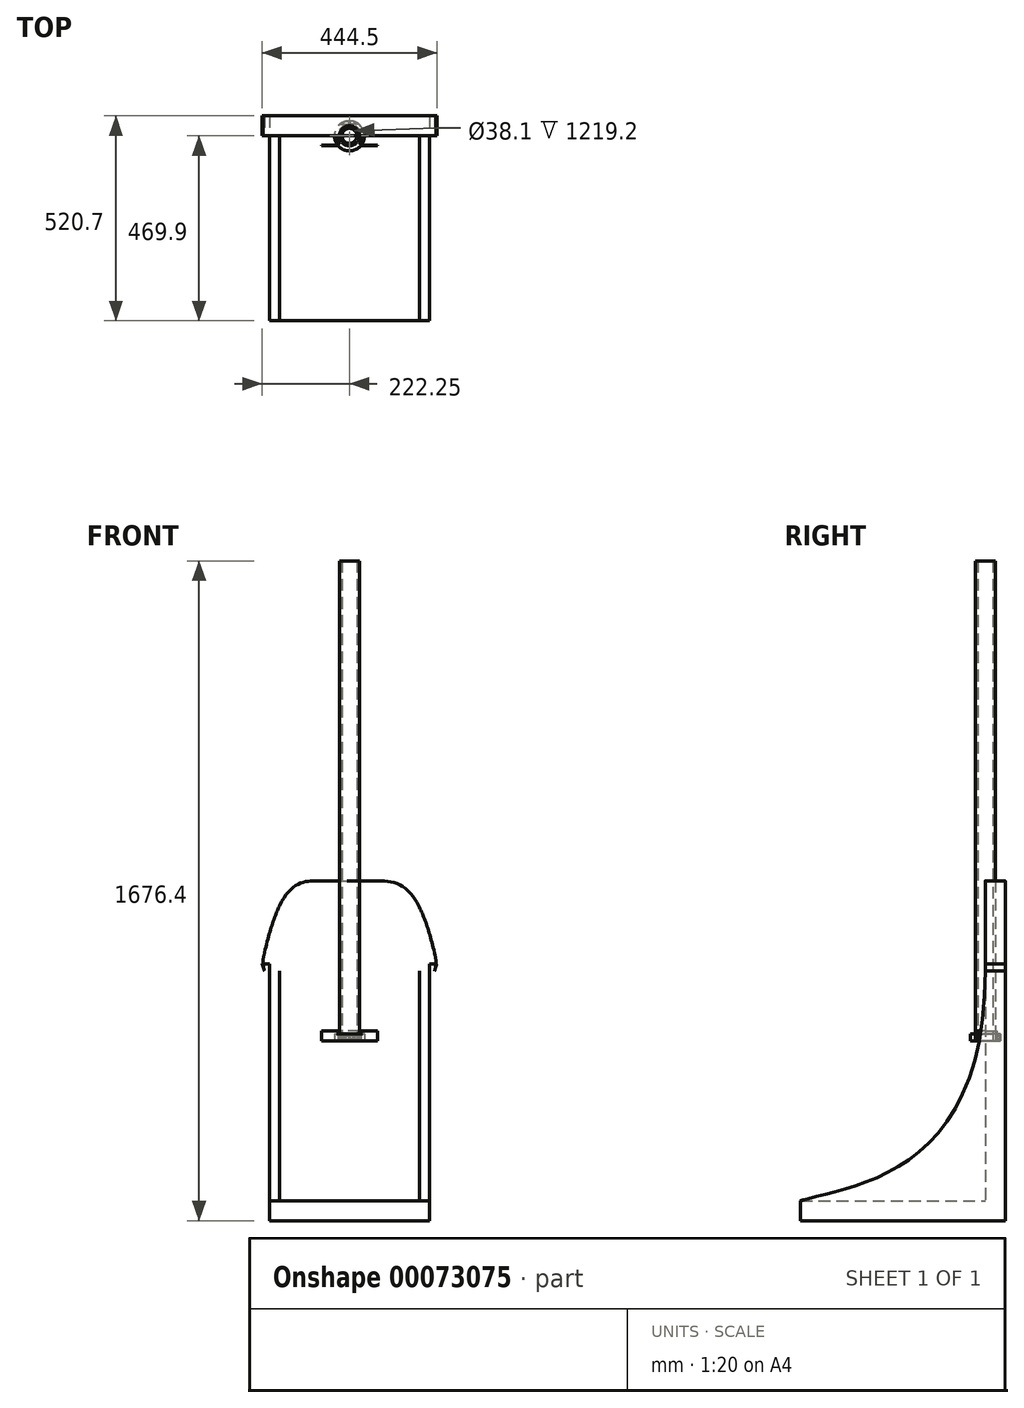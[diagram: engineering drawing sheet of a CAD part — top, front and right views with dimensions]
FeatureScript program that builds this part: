
annotation { "Feature Type Name" : "Feature", "Feature Type Description" : "" }
export const myFeature = defineFeature(function(context is Context, id is Id, definition is map)
    precondition{}
    {
        {
            var Q0;
            Q0=qCreatedBy(makeId("Top.planeOp"),FACE);
            var sketch = newSketch(context, id + "F0", { "sketchPlane" : qUnion([Q0])});
            skCircle(sketch, "E0", {"center": v(0, 0) * mm, "radius": 25.4 * mm});
            skCircle(sketch, "E1", {"center": v(0, 0) * mm, "radius": 19.05 * mm});
            skLineSegment(sketch, "E2", {"start": v(-26.99, 0) * mm, "end": v(-26.99, -19.05) * mm});
            skLineSegment(sketch, "E3", {"start": v(26.99, 0) * mm, "end": v(26.99, -19.05) * mm});
            skLineSegment(sketch, "E4", {"start": v(33.34, -25.4) * mm, "end": v(71.44, -25.4) * mm});
            skLineSegment(sketch, "E5", {"start": v(-33.34, -25.4) * mm, "end": v(-71.44, -25.4) * mm});
            skArc(sketch, "E6", {"start": v(-26.99, 0) * mm, "mid": v(0, 26.99) * mm, "end": v(26.99, 0) * mm});
            skPoint(sketch, "E7.visualSharp", {"position": v(-26.99, -25.4) * mm});
            skArc(sketch, "E7.filletArc", {"start": v(-33.34, -25.4) * mm, "mid": v(-28.85, -23.54) * mm, "end": v(-26.99, -19.05) * mm});
            skPoint(sketch, "E8.visualSharp", {"position": v(26.99, -25.4) * mm});
            skArc(sketch, "E8.filletArc", {"start": v(26.99, -19.05) * mm, "mid": v(28.85, -23.54) * mm, "end": v(33.34, -25.4) * mm});
            skArc(sketch, "E9.1", {"start": v(33.14, -19.05) * mm, "mid": v(33.2, -19.19) * mm, "end": v(33.34, -19.24) * mm});
            skArc(sketch, "E9.4", {"start": v(-33.34, -19.24) * mm, "mid": v(-33.2, -19.19) * mm, "end": v(-33.14, -19.05) * mm});
            skLineSegment(sketch, "E10.0", {"start": v(33.34, -23.16) * mm, "end": v(71.44, -23.16) * mm});
            skArc(sketch, "E10.1", {"start": v(29.23, -19.05) * mm, "mid": v(30.43, -21.95) * mm, "end": v(33.34, -23.16) * mm});
            skLineSegment(sketch, "E10.2", {"start": v(29.23, 0) * mm, "end": v(29.23, -19.05) * mm});
            skLineSegment(sketch, "E10.3", {"start": v(-33.34, -23.16) * mm, "end": v(-71.44, -23.16) * mm});
            skArc(sketch, "E10.4", {"start": v(-33.34, -23.16) * mm, "mid": v(-30.43, -21.95) * mm, "end": v(-29.23, -19.05) * mm});
            skLineSegment(sketch, "E10.5", {"start": v(-29.23, 0) * mm, "end": v(-29.23, -19.05) * mm});
            skArc(sketch, "E10.6", {"start": v(-29.23, 0) * mm, "mid": v(0, 29.23) * mm, "end": v(29.23, 0) * mm});
            skLineSegment(sketch, "E11", {"start": v(71.44, -23.16) * mm, "end": v(71.44, -25.4) * mm});
            skLineSegment(sketch, "E12", {"start": v(-71.44, -23.16) * mm, "end": v(-71.44, -25.4) * mm});
            skSolve(sketch);
        }
        {
            var Q0;
            Q0=makeQuery(id+"F0.imprint","IMPRINT",FACE,{"disambiguationData":[TD([[makeQuery(id+"F0.imprint","IMPRINT",EDGE,{"derivedFrom":sQuery(id+"F0.wireOp",EDGE,"E0")}),1.0]])]});
            extrude(context, id + "F1", {"entities" : qUnion([Q0]), "depth" : 1219.2 * mm});
        }
        {
            var Q0;
            Q0=makeQuery(id+"F0.imprint","IMPRINT",FACE,{"disambiguationData":[TD([[makeQuery(id+"F0.imprint","IMPRINT",EDGE,{"derivedFrom":sQuery(id+"F0.wireOp",EDGE,"E2")}),-1.0]])]});
            extrude(context, id + "F2", {"entities" : qUnion([Q0]), "depth" : 25.4 * mm});
        }
        {
            var Q0;
            Q0=qCreatedBy(makeId("Top.planeOp"),FACE);
            var sketch = newSketch(context, id + "F3", { "sketchPlane" : qUnion([Q0])});
            skArc(sketch, "E13", {"start": v(-1.21, 38.08) * mm, "mid": v(0, -38.1) * mm, "end": v(1.21, 38.08) * mm});
            skArc(sketch, "E14", {"start": v(-1.21, 25.37) * mm, "mid": v(0, -25.4) * mm, "end": v(1.21, 25.37) * mm});
            skLineSegment(sketch, "E15", {"start": v(1.21, 38.08) * mm, "end": v(1.21, 25.37) * mm});
            skLineSegment(sketch, "E16", {"start": v(-1.21, 38.08) * mm, "end": v(-1.21, 25.37) * mm});
            skSolve(sketch);
        }
        {
            var Q0;
            Q0=makeQuery(id+"F3.imprint","IMPRINT",FACE,{"disambiguationData":[TD([[makeQuery(id+"F3.imprint","IMPRINT",EDGE,{"derivedFrom":sQuery(id+"F3.wireOp",EDGE,"E13")}),1.0]])]});
            extrude(context, id + "F4", {"entities" : qUnion([Q0]), "depth" : 17.48 * mm});
        }
        {
            var Q0;
            Q0=qCreatedBy(makeId("Right.planeOp"),FACE);
            var sketch = newSketch(context, id + "F5", { "sketchPlane" : qUnion([Q0])});
            skCircle(sketch, "E17", {"center": v(33.29, 8.78) * mm, "radius": 3.81 * mm});
            skPoint(sketch, "E17.first.point", {"position": v(37.1, 8.75) * mm});
            skPoint(sketch, "E17.second.point", {"position": v(29.48, 8.75) * mm});
            skPoint(sketch, "E17.third.point", {"position": v(30.58, 11.46) * mm});
            skSolve(sketch);
        }
        {
            var Q0;
            Q0=sQuery(id+"F5.wireOp",VERTEX,"E17.center");
            var Q1;
            Q1=makeQuery(id+"F4.opExtrude","SWEPT_BODY",BODY,{"disambiguationData":[OSD([sQuery(id+"F3.wireOp",EDGE,"E13"),sQuery(id+"F3.wireOp",EDGE,"E14"),sQuery(id+"F3.wireOp",EDGE,"E15"),sQuery(id+"F3.wireOp",EDGE,"E16")])]});
            hole(context, id + "F6", {"style" : HoleStyle.SIMPLE, "holeDiameter" : 7.62 * mm, "endStyle" : HoleEndStyle.THROUGH, "locations" : qUnion([Q0]), "scope" : qUnion([Q1])});
        }
        {
            var Q0;
            Q0=sQuery(id+"F5.wireOp",VERTEX,"E17.center");
            var Q1;
            Q1=makeQuery(id+"F4.opExtrude","SWEPT_BODY",BODY,{"disambiguationData":[OSD([sQuery(id+"F3.wireOp",EDGE,"E13"),sQuery(id+"F3.wireOp",EDGE,"E14"),sQuery(id+"F3.wireOp",EDGE,"E15"),sQuery(id+"F3.wireOp",EDGE,"E16")])]});
            hole(context, id + "F7", {"style" : HoleStyle.SIMPLE, "holeDiameter" : 7.62 * mm, "endStyle" : HoleEndStyle.THROUGH, "oppositeDirection" : true, "locations" : qUnion([Q0]), "scope" : qUnion([Q1])});
        }
        {
            var Q0;
            Q0=qCreatedBy(makeId("Front.planeOp"),FACE);
            var sketch = newSketch(context, id + "F8", { "sketchPlane" : qUnion([Q0])});
            skLineSegment(sketch, "E18.rect.bottom", {"start": v(177.8, 406.4) * mm, "end": v(-177.8, 406.4) * mm});
            skLineSegment(sketch, "E18.rect.top", {"start": v(177.8, -406.4) * mm, "end": v(-177.8, -406.4) * mm});
            skLineSegment(sketch, "E18.rect.left", {"start": v(177.8, 406.4) * mm, "end": v(177.8, -406.4) * mm});
            skLineSegment(sketch, "E18.rect.right", {"start": v(-177.8, 406.4) * mm, "end": v(-177.8, -406.4) * mm});
            skPoint(sketch, "E18.rect.middle", {"position": v(0, 0) * mm});
            skLineSegment(sketch, "E19", {"start": v(-177.8, -406.4) * mm, "end": v(-177.8, -457.2) * mm});
            skLineSegment(sketch, "E20", {"start": v(-177.8, -457.2) * mm, "end": v(177.8, -457.2) * mm});
            skLineSegment(sketch, "E21", {"start": v(177.8, -457.2) * mm, "end": v(177.8, -406.4) * mm});
            skLineSegment(sketch, "E22", {"start": v(0, 195.28) * mm, "end": v(222.25, 195.28) * mm});
            skLineSegment(sketch, "E23", {"start": v(0, 195.28) * mm, "end": v(-222.25, 195.28) * mm});
            skFitSpline(sketch, "E24", {"points": [v(222.25, 195.28) * mm, v(177.8, -406.4) * mm], "startDerivative": vector(-133.35, -351.52) * mm, "endDerivative": vector(-44.45, -601.68) * mm});
            skFitSpline(sketch, "E25", {"points": [v(-222.25, 195.28) * mm, v(-177.8, -406.4) * mm], "startDerivative": vector(133.35, -334.43) * mm, "endDerivative": vector(44.45, -601.68) * mm});
            skFitSpline(sketch, "E26", {"points": [v(-222.25, 195.28) * mm, v(-73.91, 406.4) * mm, v(63.57, 406.4) * mm, v(222.25, 195.28) * mm], "startDerivative": vector(365.6, 1736.47) * mm, "endDerivative": vector(361.37, -1716.37) * mm});
            skArc(sketch, "E27.filletArc", {"start": v(-217.57, 216.72) * mm, "mid": v(-219.4, 197.15) * mm, "end": v(-216.17, 177.77) * mm});
            skArc(sketch, "E28.filletArc", {"start": v(216.4, 177.8) * mm, "mid": v(219.5, 197.03) * mm, "end": v(217.62, 216.4) * mm});
            skSolve(sketch);
        }
        {
            var Q0;
            {var subQ5=sQuery(id+"F8.wireOp",EDGE,"E26");var subQ6=sQuery(id+"F8.wireOp",EDGE,"E18.rect.left");var subQ7=makeQuery(id+"F8.imprint","INTERSECT",VERTEX,{"derivedFrom":[subQ6,subQ5]});Q0=makeQuery(id+"F8.imprint","IMPRINT",FACE,{"disambiguationData":[TD([[makeQuery(id+"F8.imprint","IMPRINT",EDGE,{"disambiguationData":[TD([[subQ7,-1.0]])],"derivedFrom":subQ6}),-1.0]])]});}
            var Q1;
            {var subQ0=sQuery(id+"F8.wireOp",EDGE,"E26");var subQ1=sQuery(id+"F8.wireOp",EDGE,"E18.rect.right");var subQ2=makeQuery(id+"F8.imprint","INTERSECT",VERTEX,{"derivedFrom":[subQ1,subQ0]});Q1=makeQuery(id+"F8.imprint","IMPRINT",FACE,{"disambiguationData":[TD([[makeQuery(id+"F8.imprint","IMPRINT",EDGE,{"disambiguationData":[TD([[subQ2,-1.0]])],"derivedFrom":subQ1}),-1.0]])]});}
            var Q2;
            {var subQ0=sQuery(id+"F8.wireOp",EDGE,"E25");Q2=makeQuery(id+"F8.imprint","IMPRINT",FACE,{"disambiguationData":[TD([[makeQuery(id+"F8.imprint","IMPRINT",EDGE,{"derivedFrom":subQ0}),1.0]])]});}
            var Q3;
            {var subQ6=sQuery(id+"F8.wireOp",EDGE,"E18.rect.top");Q3=makeQuery(id+"F8.imprint","IMPRINT",FACE,{"disambiguationData":[TD([[makeQuery(id+"F8.imprint","IMPRINT",EDGE,{"derivedFrom":subQ6}),-1.0]])]});}
            var Q4;
            {var subQ0=sQuery(id+"F8.wireOp",EDGE,"E26");var subQ1=sQuery(id+"F8.wireOp",EDGE,"E18.rect.left");var subQ2=makeQuery(id+"F8.imprint","INTERSECT",VERTEX,{"derivedFrom":[subQ1,subQ0]});Q4=makeQuery(id+"F8.imprint","IMPRINT",FACE,{"disambiguationData":[TD([[makeQuery(id+"F8.imprint","IMPRINT",EDGE,{"disambiguationData":[TD([[subQ2,-1.0]])],"derivedFrom":subQ1}),1.0]])]});}
            var Q5;
            {var subQ0=sQuery(id+"F8.wireOp",EDGE,"E24");Q5=makeQuery(id+"F8.imprint","IMPRINT",FACE,{"disambiguationData":[TD([[makeQuery(id+"F8.imprint","IMPRINT",EDGE,{"derivedFrom":subQ0}),-1.0]])]});}
            var Q6;
            Q6=makeQuery(id+"F8.imprint","IMPRINT",FACE,{"disambiguationData":[TD([[makeQuery(id+"F8.imprint","IMPRINT",EDGE,{"derivedFrom":sQuery(id+"F8.wireOp",EDGE,"E18.rect.top")}),1.0]])]});
            extrude(context, id + "F9", {"entities" : qUnion([Q0, Q1, Q2, Q3, Q4, Q5, Q6]), "oppositeDirection" : true, "depth" : 50.8 * mm});
        }
        {
            var Q0;
            {var subQ0=sQuery(id+"F8.wireOp",EDGE,"E21");Q0=makeQuery(id+"F11.boolean.opBoolean","MERGE",FACE,{"derivedFrom":[makeQuery(id+"F9.opExtrude","SWEPT_FACE",FACE,{"disambiguationData":[OSD([subQ0])]}),makeQuery(id+"F11.opExtrude","SWEPT_FACE",FACE,{"disambiguationData":[OSD([subQ0])]})]});}
            var sketch = newSketch(context, id + "F10", { "sketchPlane" : qUnion([Q0])});
            skFitSpline(sketch, "E29", {"points": [v(0, 177.78) * mm, v(-469.9, -406.4) * mm], "startDerivative": vector(0, -1545.1) * mm, "endDerivative": vector(-426.97, -118.06) * mm});
            skLineSegment(sketch, "E30", {"start": v(0, 177.78) * mm, "end": v(50.8, 177.78) * mm});
            skLineSegment(sketch, "E31", {"start": v(50.8, 177.78) * mm, "end": v(50.8, -406.4) * mm});
            skLineSegment(sketch, "E32", {"start": v(50.8, -406.4) * mm, "end": v(-469.9, -406.4) * mm});
            skSolve(sketch);
        }
        {
            var Q0;
            Q0=makeQuery(id+"F8.imprint","IMPRINT",FACE,{"disambiguationData":[TD([[makeQuery(id+"F8.imprint","IMPRINT",EDGE,{"derivedFrom":sQuery(id+"F8.wireOp",EDGE,"E18.rect.top")}),1.0]])]});
            extrude(context, id + "F11", {"entities" : qUnion([Q0]), "operationType" : NewBodyOperationType.ADD, "depth" : 469.9 * mm});
        }
        {
            var Q0;
            {var subQ0=sQuery(id+"F8.wireOp",EDGE,"E21");Q0=makeQuery(id+"F11.boolean.opBoolean","MERGE",FACE,{"derivedFrom":[makeQuery(id+"F9.opExtrude","SWEPT_FACE",FACE,{"disambiguationData":[OSD([subQ0])]}),makeQuery(id+"F11.opExtrude","SWEPT_FACE",FACE,{"disambiguationData":[OSD([subQ0])]})]});}
            var Q1;
            {var subQ0=sQuery(id+"F8.wireOp",EDGE,"E19");Q1=makeQuery(id+"F11.boolean.opBoolean","MERGE",FACE,{"derivedFrom":[makeQuery(id+"F9.opExtrude","SWEPT_FACE",FACE,{"disambiguationData":[OSD([subQ0])]}),makeQuery(id+"F11.opExtrude","SWEPT_FACE",FACE,{"disambiguationData":[OSD([subQ0])]})]});}
            extrude(context, id + "F12", {"entities" : qUnion([Q0, Q1]), "operationType" : NewBodyOperationType.ADD, "endBound" : BoundingType.SYMMETRIC, "depth" : 50.8 * mm});
        }
        {
            var Q0;
            Q0=makeQuery(id+"F12.opExtrude","CAP_FACE",FACE,{"disambiguationData":[OSD([sQuery(id+"F8.wireOp",EDGE,"E19")])],"isStart":true});
            var sketch = newSketch(context, id + "F13", { "sketchPlane" : qUnion([Q0])});
            skLineSegment(sketch, "E33", {"start": v(-50.8, 177.26) * mm, "end": v(-50.8, -406.4) * mm});
            skFitSpline(sketch, "E34.MirrorCS", {"points": [v(0, 177.26) * mm, v(469.9, -406.4) * mm], "startDerivative": vector(0, -1544.08) * mm, "endDerivative": vector(426.97, -118.06) * mm});
            skLineSegment(sketch, "E35", {"start": v(-50.8, 177.26) * mm, "end": v(0, 177.26) * mm});
            skLineSegment(sketch, "E36", {"start": v(469.9, -406.4) * mm, "end": v(-50.8, -406.4) * mm});
            skSolve(sketch);
        }
        {
            var Q0;
            {var subQ4=sQuery(id+"F10.wireOp",EDGE,"E29");Q0=makeQuery(id+"F10.imprint","IMPRINT",FACE,{"disambiguationData":[TD([[makeQuery(id+"F10.imprint","IMPRINT",EDGE,{"derivedFrom":subQ4}),1.0]])]});}
            extrude(context, id + "F14", {"entities" : qUnion([Q0]), "operationType" : NewBodyOperationType.ADD, "depth" : 25.4 * mm});
        }
        {
            var Q0;
            Q0 = qSketchRegion(id + "F13", true);
            extrude(context, id + "F15", {"entities" : qUnion([Q0]), "operationType" : NewBodyOperationType.ADD, "oppositeDirection" : true, "depth" : 25.4 * mm});
        }
    });
